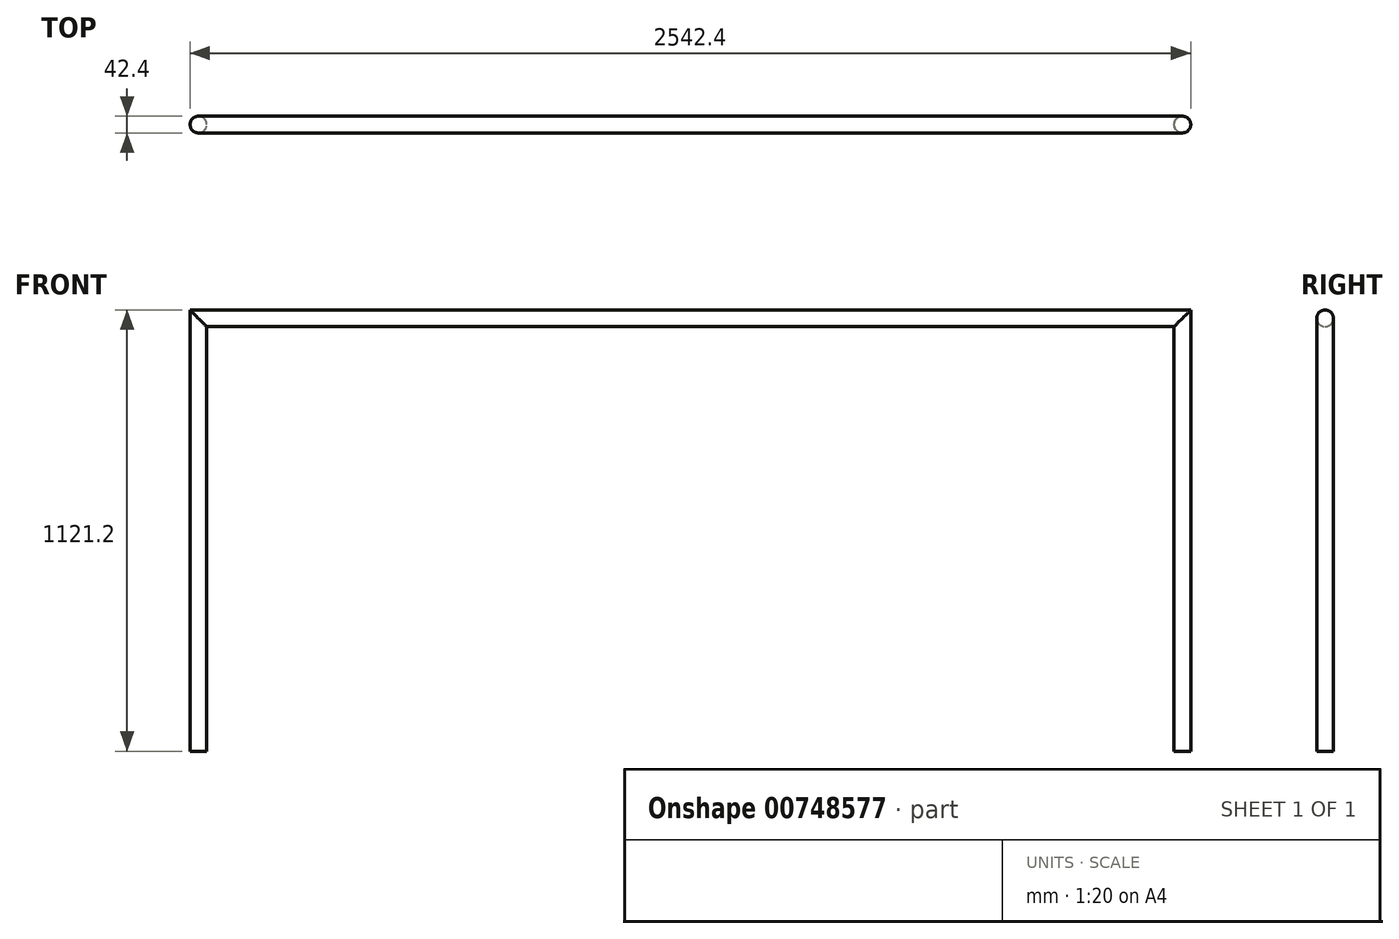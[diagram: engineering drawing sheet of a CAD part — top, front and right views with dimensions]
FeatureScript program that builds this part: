
annotation { "Feature Type Name" : "Feature", "Feature Type Description" : "" }
export const myFeature = defineFeature(function(context is Context, id is Id, definition is map)
    precondition{}
    {
        {
            var Q0;
            Q0=qCreatedBy(makeId("Front.planeOp"),FACE);
            var sketch = newSketch(context, id + "F0", { "sketchPlane" : qUnion([Q0])});
            skLineSegment(sketch, "E0", {"start": v(0, 0) * mm, "end": v(0, 1100) * mm});
            skLineSegment(sketch, "E1", {"start": v(0, 1100) * mm, "end": v(2500, 1100) * mm});
            skLineSegment(sketch, "E2", {"start": v(2500, 1100) * mm, "end": v(2500, 0) * mm});
            skLineSegment(sketch, "E3", {"start": v(833.33, 1100) * mm, "end": v(833.33, 0) * mm});
            skLineSegment(sketch, "E4", {"start": v(1666.67, 1100) * mm, "end": v(1666.67, 0) * mm});
            skLineSegment(sketch, "E5", {"start": v(0, 880) * mm, "end": v(2500, 880) * mm});
            skLineSegment(sketch, "E6", {"start": v(0, 660) * mm, "end": v(2500, 660) * mm});
            skLineSegment(sketch, "E7", {"start": v(0, 440) * mm, "end": v(2500, 440) * mm});
            skLineSegment(sketch, "E8", {"start": v(0, 220) * mm, "end": v(2500, 220) * mm});
            skSolve(sketch);
        }
        {
            var Q0;
            Q0=qCreatedBy(makeId("Top.planeOp"),FACE);
            var sketch = newSketch(context, id + "F1", { "sketchPlane" : qUnion([Q0])});
            skCircle(sketch, "E9", {"center": v(0, 0) * mm, "radius": 21.2 * mm});
            skSolve(sketch);
        }
        {
            var Q0;
            Q0=makeQuery(id+"F1.imprint","IMPRINT",FACE,{"disambiguationData":[TD([[makeQuery(id+"F1.imprint","IMPRINT",EDGE,{"derivedFrom":sQuery(id+"F1.wireOp",EDGE,"E9")}),1.0]])]});
            var Q1;
            Q1=sQuery(id+"F0.wireOp",EDGE,"E0");
            var Q2;
            Q2=sQuery(id+"F0.wireOp",EDGE,"E1");
            var Q3;
            Q3=sQuery(id+"F0.wireOp",EDGE,"E2");
            sweep(context, id + "F2", {"profiles" : qUnion([Q0]), "path" : qUnion([Q1, Q2, Q3])});
        }
    });
